# Revit family: Grohe_PlumbingFixtures_ConcealedBody_Euroeco_36337001a
name_source: partatom
category: Plumbing Fixtures
revit_build: Autodesk Revit 2017 (Build: 20190508_0315(x64)
units: mm (PartAtom-declared; Revit-internal decimal feet)

## family parameters
Cut with Voids When Loaded = No
Host = Face
OmniClass Number = 23.65.00.00
OmniClass Title = Supply and Distribution of Liquids and Gases
Part Type = Normal
Room Calculation Point = No
Round Connector Dimension = Use Diameter
Shared = No

## types (1)
- 36337001
    ADACompliant = No
    Assembly Code = C1030
    AssetType = Fixed
    BIMObjectName = Grohe_PlumbingFixtures_ConcealedBody_Euroeco_36337001
    CW Connection = Yes
    CWFU = 4.5
    ClassificationName = Uniclass2015
    ClassificationValue = Pr_40_20_87_80
    ColdWaterConnectionDiameter = 10 mm  [stored 0.0328084 ft]
    Color = Blue
    Cost = 0 $
    Default Elevation = 0 mm  [stored 0 ft]
    Description = wall installation. for installation with pre-mixed or cold water. suitable for IR-sets for final installation. stop valve. connection housing for power supply. suitable for. 36 410 000, 36 334 SD0, 36 335 SD0, 36 273 000. allows for waterproofing of wall construction surrounding the concealed body. with sealing sleeve.
    DocumentationCertificates = https://www.grohe.com
    DocumentationInstallationGuide = https://www.grohe.com
    DocumentationLiterature = https://www.grohe.com
    DocumentationMaintenance = https://www.grohe.com
    DocumentationTechnical = https://www.grohe.com
    DurationUnit = Years
    Ecojoy = No
    ExpectedLife = 0
    FaucetMaterial = Plastic, Opaque Dark Blue
    Features = wall installation. for installation with pre-mixed or cold water. suitable for IR-sets for final installation. stop valve. connection housing for power supply. suitable for. 36 410 000, 36 334 SD0, 36 335 SD0, 36 273 000. allows for waterproofing of wall construction surrounding the concealed body. with sealing sleeve.
    HW Connection = Yes
    HWFU = 4.5
    HotWaterConnectionDiameter = 10 mm  [stored 0.0328084 ft]
    IfcExportAs = IfcPipeFitting
    IfcExportType = IfcPipeFittingType
    Keynote = N13
    LowEmittingMaterial = No
    Manufacturer = Grohe
    ManufacturerName = Grohe
    MasterformatNumber = 01 52 19
    MasterformatTitle = Sanitary Facilities
    Model = Euroeco Cosmopolitan E Concealed mounting box
    ModelNumber = 36337001
    ModelReference = Euroeco Cosmopolitan E Concealed mounting box
    NBSDescription = Shower thermostatic valves
    NBSObjectName = Grohe - Shower thermostatic valves
    NBSReference = 45-35-70/335
    NominalDepth = 0 mm  [stored 0 ft]
    NominalHeight = 0 mm  [stored 0 ft]
    NominalLength = 0 mm  [stored 0 ft]
    ProductionYear = 2020
    Type Comments = 36337001
    TypeName = 36337001
    URL = https://www.grohe.com
    Vent Connection = No
    WarrantyDurationLabor = 0
    WarrantyDurationParts = 0
    WarrantyDurationUnit = Years
    Waste Connection = No
    _BSBibleVersion = 15
    _BimSpecGuid = 0
    _CurrentRevision = 1
    _DistributedBy = www.bimstore.co

note: [stored X ft] marks values corroborated as IEEE doubles in the binary element streams (Revit-internal decimal feet)

## geometry (parser evidence)
native form markers: Blend x2, Sweep x3
no freeform markers — native parametric forms only
